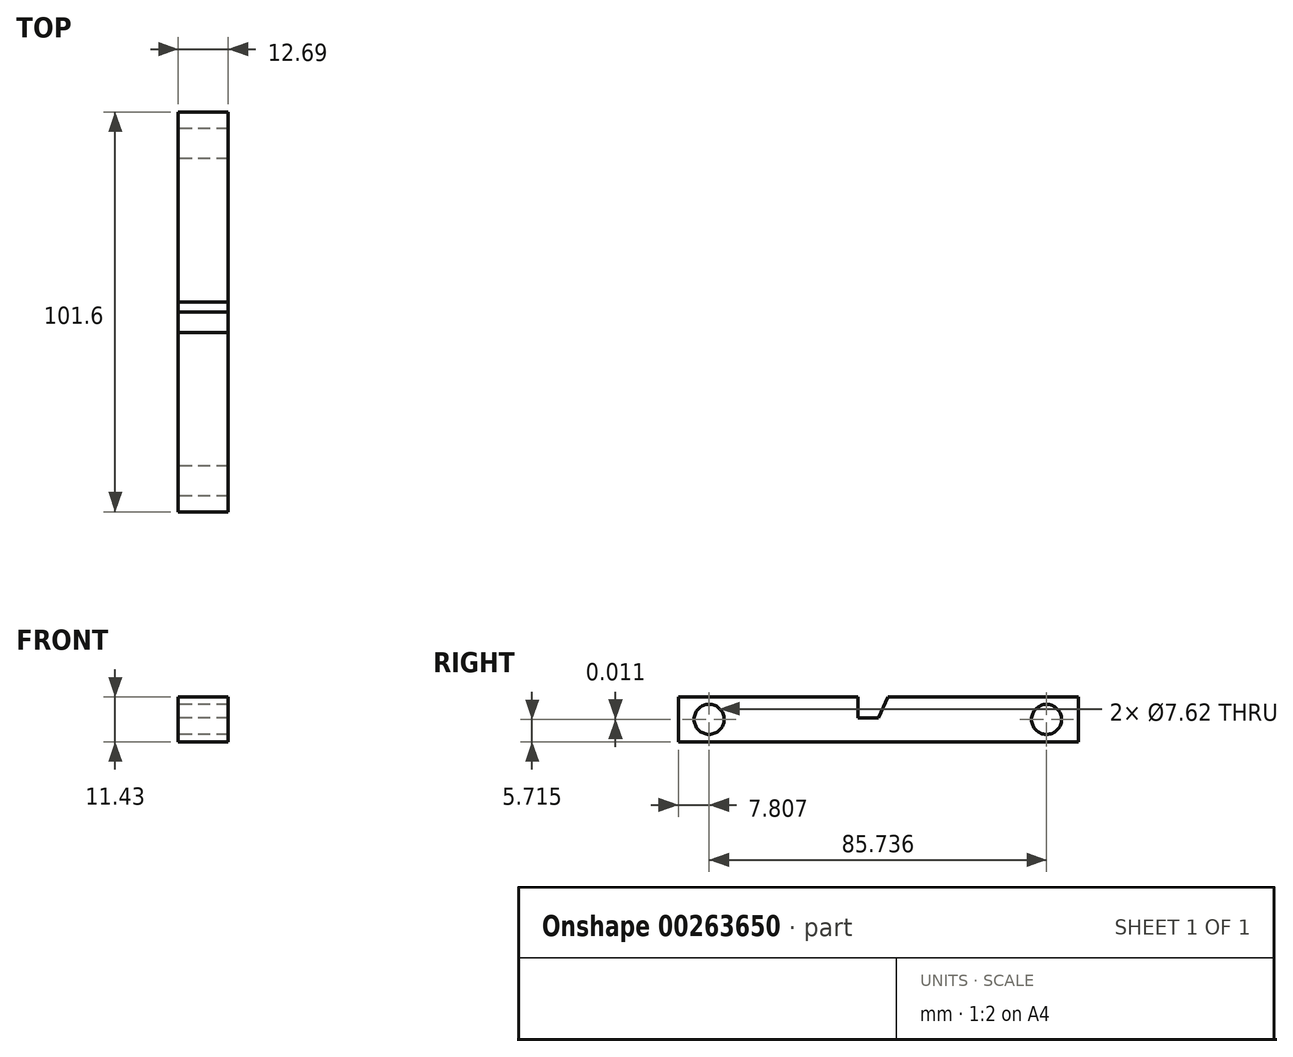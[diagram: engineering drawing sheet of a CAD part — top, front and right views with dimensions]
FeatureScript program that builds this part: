
annotation { "Feature Type Name" : "Feature", "Feature Type Description" : "" }
export const myFeature = defineFeature(function(context is Context, id is Id, definition is map)
    precondition{}
    {
        {
            var Q0;
            Q0=qCreatedBy(makeId("Front.planeOp"),FACE);
            var sketch = newSketch(context, id + "F0", { "sketchPlane" : qUnion([Q0])});
            skLineSegment(sketch, "E0", {"start": v(0, 0) * mm, "end": v(-12.7, 0) * mm});
            skLineSegment(sketch, "E1", {"start": v(-12.7, 0) * mm, "end": v(-12.7, 11.43) * mm});
            skLineSegment(sketch, "E2", {"start": v(-12.7, 11.43) * mm, "end": v(0, 11.43) * mm});
            skLineSegment(sketch, "E3", {"start": v(0, 11.43) * mm, "end": v(0, 0) * mm});
            skSolve(sketch);
        }
        {
            var Q0;
            Q0=makeQuery(id+"F0.imprint","IMPRINT",FACE,{"disambiguationData":[TD([[makeQuery(id+"F0.imprint","IMPRINT",EDGE,{"derivedFrom":sQuery(id+"F0.wireOp",EDGE,"E0")}),-1.0]])]});
            extrude(context, id + "F1", {"entities" : qUnion([Q0]), "depth" : 101.6 * mm});
        }
        {
            var Q0;
            Q0=makeQuery(id+"F1.opExtrude","SWEPT_FACE",FACE,{"disambiguationData":[OSD([sQuery(id+"F0.wireOp",EDGE,"E1")])]});
            var sketch = newSketch(context, id + "F2", { "sketchPlane" : qUnion([Q0])});
            skLineSegment(sketch, "E4", {"start": v(48.3, 11.43) * mm, "end": v(50.8, 6.04) * mm});
            skPoint(sketch, "E4.endSnap0", {"position": v(50.8, 11.43) * mm});
            skLineSegment(sketch, "E5", {"start": v(50.8, 6.04) * mm, "end": v(56.03, 6.04) * mm});
            skLineSegment(sketch, "E6", {"start": v(56.03, 6.04) * mm, "end": v(56.03, 11.43) * mm});
            skLineSegment(sketch, "E7", {"start": v(56.03, 11.43) * mm, "end": v(50.8, 11.43) * mm});
            skLineSegment(sketch, "E8", {"start": v(48.3, 11.43) * mm, "end": v(50.8, 11.43) * mm});
            skSolve(sketch);
        }
        {
            var Q0;
            Q0 = qSketchRegion(id + "F2", true);
            extrude(context, id + "F3", {"entities" : qUnion([Q0]), "operationType" : NewBodyOperationType.REMOVE, "oppositeDirection" : true, "depth" : 25.4 * mm});
        }
        {
            var Q0;
            Q0=makeQuery(id+"F1.opExtrude","SWEPT_FACE",FACE,{"disambiguationData":[OSD([sQuery(id+"F0.wireOp",EDGE,"E1")])]});
            var sketch = newSketch(context, id + "F4", { "sketchPlane" : qUnion([Q0])});
            skLineSegment(sketch, "E9", {"start": v(0, 5.72) * mm, "end": v(8.06, 5.72) * mm});
            skSolve(sketch);
        }
        {
            var Q0;
            {var subQ2=sQuery(id+"F0.wireOp",EDGE,"E1");Q0=makeQuery(id+"F4.imprint","IMPRINT",FACE,{"disambiguationData":[TD([[makeQuery(id+"F4.imprint","IMPRINT",EDGE,{"derivedFrom":makeQuery(id+"F1.opExtrude","CAP_EDGE",EDGE,{"disambiguationData":[OSD([subQ2])],"isStart":false})}),1.0]])]});}
            var sketch = newSketch(context, id + "F5", { "sketchPlane" : qUnion([Q0])});
            skLineSegment(sketch, "E10", {"start": v(101.85, 5.73) * mm, "end": v(93.8, 5.73) * mm});
            skSolve(sketch);
        }
        {
            var Q0;
            Q0=sQuery(id+"F4.wireOp",VERTEX,"E9.end");
            var Q1;
            Q1=makeQuery(id+"F1.opExtrude","SWEPT_BODY",BODY,{"disambiguationData":[OSD([sQuery(id+"F0.wireOp",EDGE,"E0"),sQuery(id+"F0.wireOp",EDGE,"E1"),sQuery(id+"F0.wireOp",EDGE,"E2"),sQuery(id+"F0.wireOp",EDGE,"E3")])]});
            hole(context, id + "F6", {"style" : HoleStyle.SIMPLE, "endStyle" : HoleEndStyle.BLIND, "holeDiameter" : 7.62 * mm, "holeDepth" : 19.05 * mm, "tappedDepth" : 12.7 * mm, "tapClearance" : 3, "locations" : qUnion([Q0]), "scope" : qUnion([Q1])});
        }
        {
            var Q0;
            Q0=sQuery(id+"F5.wireOp",VERTEX,"E10.end");
            var Q1;
            Q1=makeQuery(id+"F1.opExtrude","SWEPT_BODY",BODY,{"disambiguationData":[OSD([sQuery(id+"F0.wireOp",EDGE,"E0"),sQuery(id+"F0.wireOp",EDGE,"E1"),sQuery(id+"F0.wireOp",EDGE,"E2"),sQuery(id+"F0.wireOp",EDGE,"E3")])]});
            hole(context, id + "F7", {"style" : HoleStyle.SIMPLE, "endStyle" : HoleEndStyle.BLIND, "holeDiameter" : 7.62 * mm, "holeDepth" : 19.05 * mm, "tappedDepth" : 12.7 * mm, "tapClearance" : 3, "locations" : qUnion([Q0]), "scope" : qUnion([Q1])});
        }
    });
